# Revit family: Medical_Equipment-Waste-Receptacle_Cart-Midmark-Synthesis1
name_source: partatom
category: Specialty Equipment
units: mm (PartAtom-declared; Revit-internal decimal feet)

## family parameters
Always vertical = Yes
Cut with Voids When Loaded = No
OmniClass Number = 23.45.30.14.14
OmniClass Title = Commercial Waste Disposal Units
Part Type = Normal
Room Calculation Point = No
Round Connector Dimension = Use Diameter
Shared = No
Work Plane-Based = No

## types (2) — shared parameters
Assembly Code = E1020810
Casework Finish = Wood - Midmark - Dark Walnut
Depth = 18.00 in
Description = Waste Receptacle - Synthesis™ Casework
Manufacturer = Midmark
Model = Midmark Synthesis Waste Receptacle - Cart
Product Documentation Link = https://www.midmark.com
Product Page URL = https://www.midmark.com
Product data url = https://bimobject.com
URL = https://www.midmark.com
Width = 18.00 in

## per-type parameters (varying)
| type | Height |
| 31" H | 31.00 in |
| 33" H | 33.00 in |

## geometry (parser evidence)
native form markers: Blend x4, Sweep x6
no freeform markers — native parametric forms only
